FCSTD DOCUMENT  (FreeCAD 1.0R39109 (Git))
Label: 000_table_assembly
License: All rights reserved
LicenseURL: http://en.wikipedia.org/wiki/All_rights_reserved
objects: App::Link×15, App::FeaturePython×4, TechDraw::DrawProjGroupItem×4, Assembly::AssemblyLink×2, TechDraw::DrawViewDimension×2, TechDraw::DrawSVGTemplate×1, Assembly::JointGroup×1, Assembly::AssemblyObject×1, TechDraw::DrawProjGroup×1, TechDraw::DrawPage×1
note: 4 computed .brp shape members not serialized (recipe doc carries the construction recipe); baked Part::Feature solids carry a one-line shape summary decoded from their .brp
EXTERNAL_REF file=020_table_top_assembly.FCStd obj=Assembly
EXTERNAL_REF file=020_table_top_assembly.FCStd obj=Body
EXTERNAL_REF file=020_table_top_assembly.FCStd obj=Body001
EXTERNAL_REF file=020_table_top_assembly.FCStd obj=Body002
EXTERNAL_REF file=020_table_top_assembly.FCStd obj=Body003
EXTERNAL_REF file=020_table_top_assembly.FCStd obj=Body004
EXTERNAL_REF file=020_table_top_assembly.FCStd obj=Body005
EXTERNAL_REF file=040_table_bottom_assembly.FCStd obj=Assembly
EXTERNAL_REF file=040_table_bottom_assembly.FCStd obj=Body
EXTERNAL_REF file=040_table_bottom_assembly.FCStd obj=Body001
EXTERNAL_REF file=040_table_bottom_assembly.FCStd obj=Body002
EXTERNAL_REF file=040_table_bottom_assembly.FCStd obj=Body003
EXTERNAL_REF file=040_table_bottom_assembly.FCStd obj=Body004
EXTERNAL_REF file=040_table_bottom_assembly.FCStd obj=Body005
EXTERNAL_REF file=040_table_bottom_assembly.FCStd obj=Body006
EXTERNAL_REF file=040_table_bottom_assembly.FCStd obj=Body007
EXTERNAL_REF file=020_table_top_assembly.FCStd obj=Body006

FEATURE [App::Link] Body
  LinkedObject = -> <external 020_table_top_assembly.FCStd>#Body
FEATURE [App::Link] Body001
  LinkPlacement = pos=(-4.64e-14,385,70) rot=(1,0,0;1.5708rad)
  LinkedObject = -> <external 020_table_top_assembly.FCStd>#Body001
  Placement = pos=(-4.64e-14,385,70) rot=(1,0,0;1.5708rad)
FEATURE [App::Link] Body002
  LinkPlacement = pos=(-2.5e-14,-385,70) rot=(0,0.707107,-0.707107;3.14159rad)
  LinkedObject = -> <external 020_table_top_assembly.FCStd>#Body002
  Placement = pos=(-2.5e-14,-385,70) rot=(0,0.707107,-0.707107;3.14159rad)
FEATURE [App::Link] Body003
  LinkPlacement = pos=(-1085,-1.269e-13,70) rot=(0.57735,-0.57735,0.57735;4.18879rad)
  LinkedObject = -> <external 020_table_top_assembly.FCStd>#Body003
  Placement = pos=(-1085,-1.269e-13,70) rot=(0.57735,-0.57735,0.57735;4.18879rad)
FEATURE [App::Link] Body004
  LinkPlacement = pos=(1085,-7.89e-14,70) rot=(0.57735,-0.57735,0.57735;4.18879rad)
  LinkedObject = -> <external 020_table_top_assembly.FCStd>#Body004
  Placement = pos=(1085,-7.89e-14,70) rot=(0.57735,-0.57735,0.57735;4.18879rad)
FEATURE [App::Link] Body005
  LinkPlacement = pos=(-940,548.179,55) rot=(0,-0.707107,0.707107;3.14159rad)
  LinkedObject = -> <external 020_table_top_assembly.FCStd>#Body005
  Placement = pos=(-940,548.179,55) rot=(0,-0.707107,0.707107;3.14159rad)
FEATURE [App::Link] Body006
  LinkedObject = -> <external 040_table_bottom_assembly.FCStd>#Body
FEATURE [App::FeaturePython] Joint  label="Distance"  # Assembly joint (typed FeaturePython)
  Activated = true
  AngleMax = 0
  AngleMin = 0
  Detach1 = false
  Detach2 = false
  Distance = 0
  Distance2 = 0
  EnableAngleMax = false
  EnableAngleMin = false
  EnableLengthMax = false
  EnableLengthMin = false
  JointType = 5 (Distance)
  LengthMax = 0
  LengthMin = 0
  Placement1 = pos=(15,15,410) rot=(0,0,1;0rad)
  Placement2 = pos=(1.42e-14,-6.25e-14,15) rot=(0,0,1;0rad)
  Reference1 = -> Assembly [Assembly002.Body006.Face9,Assembly002.Body006.Face9]
  Reference2 = -> Assembly [Assembly001.Body.Face6,Assembly001.Body.Vertex2]
FEATURE [App::FeaturePython] Joint001  label="Distance001"  # Assembly joint (typed FeaturePython)
  Activated = true
  AngleMax = 0
  AngleMin = 0
  Detach1 = false
  Detach2 = false
  Distance = 0
  Distance2 = 0
  EnableAngleMax = false
  EnableAngleMin = false
  EnableLengthMax = false
  EnableLengthMin = false
  JointType = 5 (Distance)
  LengthMax = 0
  LengthMin = 0
  Placement1 = pos=(15,-20,355) rot=(1,0,0;1.5708rad)
  Placement2 = pos=(-1.23163,0,15) rot=(0,0,1;0rad)
  Reference1 = -> Assembly [Assembly002.Body006.Face8,Assembly002.Body006.Face8]
  Reference2 = -> Assembly [Assembly001.Body001.Face5,Assembly001.Body001.Vertex4]
FEATURE [App::FeaturePython] Joint002  label="Distance002"  # Assembly joint (typed FeaturePython)
  Activated = true
  AngleMax = 0
  AngleMin = 0
  Detach1 = false
  Detach2 = false
  Distance = 0
  Distance2 = 0
  EnableAngleMax = false
  EnableAngleMin = false
  EnableLengthMax = false
  EnableLengthMin = false
  JointType = 5 (Distance)
  LengthMax = 0
  LengthMin = 0
  Placement1 = pos=(-20,15,355) rot=(-0.57735,0.57735,0.57735;4.18879rad)
  Placement2 = pos=(5.9e-15,0,15) rot=(0,0,1;0rad)
  Reference1 = -> Assembly [Assembly002.Body006.Face7,Assembly002.Body006.Face7]
  Reference2 = -> Assembly [Assembly001.Body003.Face6,Assembly001.Body003.Vertex2]
FEATURE [App::Link] Body007
  LinkPlacement = pos=(-3.39e-14,700,-2.35e-14) rot=(0,0,1;4.71239rad)
  LinkedObject = -> <external 040_table_bottom_assembly.FCStd>#Body001
  Placement = pos=(-3.39e-14,700,-2.35e-14) rot=(0,0,1;4.71239rad)
FEATURE [App::Link] Body008
  LinkPlacement = pos=(1770,8.9e-15,1.22e-14) rot=(0,0,1;1.5708rad)
  LinkedObject = -> <external 040_table_bottom_assembly.FCStd>#Body002
  Placement = pos=(1770,8.9e-15,1.22e-14) rot=(0,0,1;1.5708rad)
FEATURE [App::Link] Body009
  LinkPlacement = pos=(1770,700,1.4038e-12) rot=(0,0,1;3.14159rad)
  LinkedObject = -> <external 040_table_bottom_assembly.FCStd>#Body003
  Placement = pos=(1770,700,1.4038e-12) rot=(0,0,1;3.14159rad)
FEATURE [TechDraw::DrawSVGTemplate] Template
  EditableTexts = approval_person=B. Hecate; creator=A. Nemesis; date_of_issue=16/08/2025; document_type=Assembly Drawing; general_tolerances=ISO 2768-m; identification_number=DN; language_code=EN; part_material=Stainless steel Mat.No. 1.4301; revision_index=AAA; sheet_number=1 / 1; sheet_scale=1 : 1; title=000_table_assembly
  Height = 297
  Orientation = 1
  Template = C:/Program Files/FreeCAD 1.0/data/Mod/TechDraw/Templates/A3_Landscape_ISO5457_minimal.svg
  Width = 420
FEATURE [App::Link] Body010
  LinkPlacement = pos=(1770,350,-260) rot=(0,-0.707107,0.707107;3.14159rad)
  LinkedObject = -> <external 040_table_bottom_assembly.FCStd>#Body004
  Placement = pos=(1770,350,-260) rot=(0,-0.707107,0.707107;3.14159rad)
FEATURE [App::Link] Body011
  LinkPlacement = pos=(2e-15,350,-260) rot=(0,-0.707107,0.707107;3.14159rad)
  LinkedObject = -> <external 040_table_bottom_assembly.FCStd>#Body005
  Placement = pos=(2e-15,350,-260) rot=(0,-0.707107,0.707107;3.14159rad)
FEATURE [App::Link] Body012
  LinkPlacement = pos=(885,-25,-260) rot=(0,1,0;1.5708rad)
  LinkedObject = -> <external 040_table_bottom_assembly.FCStd>#Body006
  Placement = pos=(885,-25,-260) rot=(0,1,0;1.5708rad)
FEATURE [App::Link] Body013
  LinkPlacement = pos=(885,725,-260) rot=(0.707107,0,-0.707107;3.14159rad)
  LinkedObject = -> <external 040_table_bottom_assembly.FCStd>#Body007
  Placement = pos=(885,725,-260) rot=(0.707107,0,-0.707107;3.14159rad)
FEATURE [Assembly::AssemblyLink] Assembly002
  Group = -> [Body006,Body007,Body008,Body009,Body010,Body011,Body012,Body013]
  LinkedObject = -> <external 040_table_bottom_assembly.FCStd>#Assembly
  Origin = -> Origin002
  Placement = pos=(-1050,350,425) rot=(1,0,0;3.14159rad)
  Rigid = true
FEATURE [App::Link] Body014
  LinkPlacement = pos=(1255.62,240,55) rot=(-0.57735,-0.57735,0.57735;2.0944rad)
  LinkedObject = -> <external 020_table_top_assembly.FCStd>#Body006
  Placement = pos=(1255.62,240,55) rot=(-0.57735,-0.57735,0.57735;2.0944rad)
FEATURE [Assembly::AssemblyLink] Assembly001
  Group = -> [Body,Body001,Body002,Body003,Body004,Body005,Body014]
  LinkedObject = -> <external 020_table_top_assembly.FCStd>#Assembly
  Origin = -> Origin001
  Rigid = true
FEATURE [App::FeaturePython] GroundedJoint  # Assembly grounded joint (typed FeaturePython)
  ObjectToGround = -> Assembly001
FEATURE [Assembly::JointGroup] Joints
  Group = -> [GroundedJoint,Joint,Joint001,Joint002]
FEATURE [Assembly::AssemblyObject] Assembly
  Group = -> [Joints,Assembly001,GroundedJoint,Assembly002,Joint,Joint001,Joint002]
  Origin = -> Origin
  Type = Assembly
FEATURE [TechDraw::DrawProjGroupItem] View  label="Front"
  CoarseView = false
  Direction = (0,-1,0)
  Focus = 100
  HardHidden = false
  IsoCount = 0
  IsoHidden = false
  IsoVisible = false
  LockPosition = true
  Perspective = false
  Rotation = 0
  RotationVector = (1,0,0)
  Scale = 0.066667
  ScaleType = 2
  ScrubCount = 1
  SeamHidden = false
  SeamVisible = true
  SmoothHidden = false
  SmoothVisible = true
  Source = -> [Assembly]
  Type = 0
  X = 0
  XDirection = (-1,0,-1e-16)
  Y = 0
FEATURE [TechDraw::DrawProjGroupItem] ProjItem  label="Right"
  CoarseView = false
  Direction = (-1,-1e-16,-1e-16)
  Focus = 100
  HardHidden = false
  IsoCount = 0
  IsoHidden = false
  IsoVisible = false
  LockPosition = false
  Perspective = false
  Rotation = 0
  RotationVector = (1,0,0)
  Scale = 0.066667
  ScaleType = 0
  ScrubCount = 1
  SeamHidden = false
  SeamVisible = true
  SmoothHidden = false
  SmoothVisible = true
  Source = -> [Assembly]
  Type = 2
  X = -128.127
  XDirection = (-1e-16,1,0)
  Y = 0
FEATURE [TechDraw::DrawProjGroupItem] ProjItem001  label="Left"
  CoarseView = false
  Direction = (1,-1e-16,1e-16)
  Focus = 100
  HardHidden = false
  IsoCount = 0
  IsoHidden = false
  IsoVisible = false
  LockPosition = false
  Perspective = false
  Rotation = 0
  RotationVector = (1,0,0)
  ScaleType = 0
  ScrubCount = 1
  SeamHidden = false
  SeamVisible = true
  SmoothHidden = false
  SmoothVisible = true
  Source = -> [Assembly]
  Type = 1
  X = 128.127
  XDirection = (-1e-16,-1,0)
  Y = 0
FEATURE [TechDraw::DrawProjGroupItem] ProjItem002  label="Bottom"
  CoarseView = false
  Direction = (-1e-16,0,1)
  Focus = 100
  HardHidden = false
  IsoCount = 0
  IsoHidden = false
  IsoVisible = false
  LockPosition = false
  Perspective = false
  Rotation = 0
  RotationVector = (1,0,0)
  ScaleType = 0
  ScrubCount = 1
  SeamHidden = false
  SeamVisible = true
  SmoothHidden = false
  SmoothVisible = true
  Source = -> [Assembly]
  Type = 5
  X = 0
  XDirection = (-1,0,-1e-16)
  Y = 76.4396
FEATURE [TechDraw::DrawProjGroup] ProjGroup
  Anchor = -> View
  AutoDistribute = true
  LockPosition = false
  ProjectionType = 0
  Rotation = 0
  Scale = 0.066667
  ScaleType = 2
  Source = -> [Assembly]
  Views = -> [View,ProjItem,ProjItem001,ProjItem002]
  X = 210.506
  Y = 148.5
  spacingX = 15
  spacingY = 15
FEATURE [TechDraw::DrawViewDimension] Dimension
  AngleOverride = false
  Arbitrary = false
  ArbitraryTolerances = false
  BoxCorners = (2) [(-73.3337,-28.3335,0),(73.3337,28.3335,0)]
  EqualTolerance = true
  ExtensionAngle = 0
  FormatSpec = %.2w
  FormatSpecOverTolerance = %+.2w
  FormatSpecUnderTolerance = %+.2w
  Inverted = false
  LineAngle = 0
  LockPosition = false
  MeasureType = 1
  OverTolerance = 0
  References2D = -> [View]
  Rotation = 0
  ScaleType = 0
  TheoreticalExact = false
  Type = 0
  UnderTolerance = 0
  X = 16.6095
  Y = -44.1973
FEATURE [TechDraw::DrawViewDimension] Dimension001
  AngleOverride = false
  Arbitrary = false
  ArbitraryTolerances = false
  BoxCorners = (2) [(-33.1061,-28.3335,0),(33.1061,28.3335,0)]
  EqualTolerance = true
  ExtensionAngle = 0
  FormatSpec = %.2w
  FormatSpecOverTolerance = %+.2w
  FormatSpecUnderTolerance = %+.2w
  Inverted = false
  LineAngle = 0
  LockPosition = false
  MeasureType = 1
  OverTolerance = 0
  References2D = -> [ProjItem001]
  Rotation = 0
  ScaleType = 0
  TheoreticalExact = false
  Type = 0
  UnderTolerance = 0
  X = 9.5557
  Y = -44.5532
FEATURE [TechDraw::DrawPage] Page
  KeepUpdated = true
  NextBalloonIndex = 1
  ProjectionType = 0
  Template = -> Template
  Views = -> [ProjGroup,Dimension,Dimension001]

RESOLVED EXTERNAL PARTS (link-assembly join: the EXTERNAL_REF files above that resolve inside this repo's crawl, each included once):
---- part 020_table_top_assembly.FCStd = doc fcstd_f8d654153843 ----
FCSTD DOCUMENT  (FreeCAD 1.0R39109 (Git))
Label: 020_table_top_assembly
License: All rights reserved
LicenseURL: http://en.wikipedia.org/wiki/All_rights_reserved
objects: App::FeaturePython×17, App::Link×7, Assembly::JointGroup×1, Assembly::AssemblyObject×1
EXTERNAL_REF file=021_table_top_sheet_30mm.FCStd obj=Body
EXTERNAL_REF file=022_table_frame_front.FCStd obj=Body
EXTERNAL_REF file=023_table_frame_back.FCStd obj=Body
EXTERNAL_REF file=025_table_frame_side_left.FCStd obj=Body
EXTERNAL_REF file=026_table_frame_side_right.FCStd obj=Body
EXTERNAL_REF file=028_table_clamp.FCStd obj=Body

FEATURE [App::Link] Body
  LinkedObject = -> <external 021_table_top_sheet_30mm.FCStd>#Body
FEATURE [App::FeaturePython] GroundedJoint  # Assembly grounded joint (typed FeaturePython)
  ObjectToGround = -> Body
FEATURE [App::Link] Body001
  LinkPlacement = pos=(-4.64e-14,385,70) rot=(1,0,0;1.5708rad)
  LinkedObject = -> <external 022_table_frame_front.FCStd>#Body
  Placement = pos=(-4.64e-14,385,70) rot=(1,0,0;1.5708rad)
FEATURE [App::Link] Body002
  LinkPlacement = pos=(-2.5e-14,-385,70) rot=(0,0.707107,-0.707107;3.14159rad)
  LinkedObject = -> <external 023_table_frame_back.FCStd>#Body
  Placement = pos=(-2.5e-14,-385,70) rot=(0,0.707107,-0.707107;3.14159rad)
FEATURE [App::FeaturePython] Joint002  label="Back1"  # Assembly joint (typed FeaturePython)
  Activated = true
  AngleMax = 0
  AngleMin = 0
  Detach1 = false
  Detach2 = false
  Distance = 0
  Distance2 = 0
  EnableAngleMax = false
  EnableAngleMin = false
  EnableLengthMax = false
  EnableLengthMin = false
  JointType = 5 (Distance)
  LengthMax = 0
  LengthMin = 0
  Placement1 = pos=(1100,-6.39e-14,-4e-16) rot=(-0.57735,-0.57735,0.57735;2.0944rad)
  Placement2 = pos=(-1100,0,0) rot=(0.57735,-0.57735,0.57735;4.18879rad)
  Reference1 = -> Assembly [Body.Face3,Body.Vertex8]
  Reference2 = -> Assembly [Body002.Face1,Body002.Face1]
FEATURE [App::FeaturePython] Joint  label="Back2"  # Assembly joint (typed FeaturePython)
  Activated = true
  AngleMax = 0
  AngleMin = 0
  Detach1 = false
  Detach2 = false
  Distance = 0
  Distance2 = 0
  EnableAngleMax = false
  EnableAngleMin = false
  EnableLengthMax = false
  EnableLengthMin = false
  JointType = 5 (Distance)
  LengthMax = 0
  LengthMin = 0
  Placement1 = pos=(1.38088,55,-0.0189681) rot=(0,-0.707107,0.707107;3.14159rad)
  Placement2 = pos=(1.42e-14,-6.25e-14,15) rot=(0,0,1;0rad)
  Reference1 = -> Assembly [Body002.Face2,Body002.Vertex7]
  Reference2 = -> Assembly [Body.Face6,Body.Vertex6]
FEATURE [App::FeaturePython] Joint003  label="Back3"  # Assembly joint (typed FeaturePython)
  Activated = true
  AngleMax = 0
  AngleMin = 0
  Detach1 = false
  Detach2 = false
  Distance = 0
  Distance2 = 0
  EnableAngleMax = false
  EnableAngleMin = false
  EnableLengthMax = false
  EnableLengthMin = false
  JointType = 5 (Distance)
  LengthMax = 0
  LengthMin = 0
  Placement1 = pos=(-1010,0,15) rot=(0,0,1;0rad)
  Placement2 = pos=(-5.37e-14,-400,-4e-16) rot=(-1,0,0;1.5708rad)
  Reference1 = -> Assembly [Body002.Face5,Body002.Face5]
  Reference2 = -> Assembly [Body.Face2,Body.Vertex6]
FEATURE [App::FeaturePython] Joint004  label="Front1"  # Assembly joint (typed FeaturePython)
  Activated = true
  AngleMax = 0
  AngleMin = 0
  Detach1 = false
  Detach2 = false
  Distance = 0
  Distance2 = 0
  EnableAngleMax = false
  EnableAngleMin = false
  EnableLengthMax = false
  EnableLengthMin = false
  JointType = 5 (Distance)
  LengthMax = 0
  LengthMin = 0
  Placement1 = pos=(-3.13e-14,-55,0) rot=(-1,0,0;1.5708rad)
  Placement2 = pos=(1.42e-14,-6.25e-14,15) rot=(0,0,1;0rad)
  Reference1 = -> Assembly [Body001.Face3,Body001.Vertex4]
  Reference2 = -> Assembly [Body.Face6,Body.Vertex8]
FEATURE [App::FeaturePython] Joint005  label="Front2"  # Assembly joint (typed FeaturePython)
  Activated = true
  AngleMax = 0
  AngleMin = 0
  Detach1 = false
  Detach2 = false
  Distance = 0
  Distance2 = 0
  EnableAngleMax = false
  EnableAngleMin = false
  EnableLengthMax = false
  EnableLengthMin = false
  JointType = 5 (Distance)
  LengthMax = 0
  LengthMin = 0
  Placement1 = pos=(5.37e-14,400,-4e-16) rot=(0,-0.707107,0.707107;3.14159rad)
  Placement2 = pos=(-1.23163,0,-15) rot=(0,0,1;0rad)
  Reference1 = -> Assembly [Body.Face4,Body.Vertex7]
  Reference2 = -> Assembly [Body001.Face4,Body001.Edge5]
FEATURE [App::FeaturePython] Joint006  label="Front3"  # Assembly joint (typed FeaturePython)
  Activated = true
  AngleMax = 0
  AngleMin = 0
  Detach1 = false
  Detach2 = false
  Distance = 0
  Distance2 = 0
  EnableAngleMax = false
  EnableAngleMin = false
  EnableLengthMax = false
  EnableLengthMin = false
  JointType = 5 (Distance)
  LengthMax = 0
  LengthMin = 0
  Placement1 = pos=(1100,-6.39e-14,-4e-16) rot=(-0.57735,-0.57735,0.57735;2.0944rad)
  Placement2 = pos=(1100,0,0) rot=(-0.57735,-0.57735,0.57735;2.0944rad)
  Reference1 = -> Assembly [Body.Face3,Body.Vertex7]
  Reference2 = -> Assembly [Body001.Face6,Body001.Face6]
FEATURE [App::Link] Body003
  LinkPlacement = pos=(-1085,-1.269e-13,70) rot=(0.57735,-0.57735,0.57735;4.18879rad)
  LinkedObject = -> <external 025_table_frame_side_left.FCStd>#Body
  Placement = pos=(-1085,-1.269e-13,70) rot=(0.57735,-0.57735,0.57735;4.18879rad)
FEATURE [App::FeaturePython] Joint008  label="Left1"  # Assembly joint (typed FeaturePython)
  Activated = true
  AngleMax = 0
  AngleMin = 0
  Detach1 = false
  Detach2 = false
  Distance = 0
  Distance2 = 0
  EnableAngleMax = false
  EnableAngleMin = false
  EnableLengthMax = false
  EnableLengthMin = false
  JointType = 5 (Distance)
  LengthMax = 0
  LengthMin = 0
  Placement1 = pos=(-3.9e-15,55,0) rot=(0,-0.707107,0.707107;3.14159rad)
  Placement2 = pos=(1.42e-14,-6.25e-14,15) rot=(0,0,1;0rad)
  Reference1 = -> Assembly [Body003.Face4,Body003.Face4]
  Reference2 = -> Assembly [Body.Face6,Body.Vertex4]
FEATURE [App::FeaturePython] Joint009  label="Left2"  # Assembly joint (typed FeaturePython)
  Activated = true
  AngleMax = 0
  AngleMin = 0
  Detach1 = false
  Detach2 = false
  Distance = 0
  Distance2 = 0
  EnableAngleMax = false
  EnableAngleMin = false
  EnableLengthMax = false
  EnableLengthMin = false
  JointType = 5 (Distance)
  LengthMax = 0
  LengthMin = 0
  Placement1 = pos=(-2.1e-15,0,-15) rot=(0,0,1;0rad)
  Placement2 = pos=(-1100,-4.97e-14,-4e-16) rot=(0.57735,-0.57735,0.57735;4.18879rad)
  Reference1 = -> Assembly [Body003.Face5,Body003.Vertex7]
  Reference2 = -> Assembly [Body.Face1,Body.Face1]
FEATURE [App::FeaturePython] Joint010  label="Left3"  # Assembly joint (typed FeaturePython)
  Activated = true
  AngleMax = 0
  AngleMin = 0
  Detach1 = false
  Detach2 = false
  Distance = 0
  Distance2 = 0
  EnableAngleMax = false
  EnableAngleMin = false
  EnableLengthMax = false
  EnableLengthMin = false
  JointType = 5 (Distance)
  LengthMax = 0
  LengthMin = 0
  Placement1 = pos=(370,-1.42e-14,0) rot=(-0.57735,-0.57735,0.57735;2.0944rad)
  Placement2 = pos=(-5e-15,0,-15) rot=(0,0,1;0rad)
  Reference1 = -> Assembly [Body003.Face3,Body003.Vertex6]
  Reference2 = -> Assembly [Body002.Face4,Body002.Vertex5]
FEATURE [App::Link] Body004
  LinkPlacement = pos=(1085,-7.89e-14,70) rot=(0.57735,-0.57735,0.57735;4.18879rad)
  LinkedObject = -> <external 026_table_frame_side_right.FCStd>#Body
  Placement = pos=(1085,-7.89e-14,70) rot=(0.57735,-0.57735,0.57735;4.18879rad)
FEATURE [App::FeaturePython] Joint011  label="Right1"  # Assembly joint (typed FeaturePython)
  Activated = true
  AngleMax = 0
  AngleMin = 0
  Detach1 = false
  Detach2 = false
  Distance = 0
  Distance2 = 0
  EnableAngleMax = false
  EnableAngleMin = false
  EnableLengthMax = false
  EnableLengthMin = false
  JointType = 5 (Distance)
  LengthMax = 0
  LengthMin = 0
  Placement1 = pos=(-4.9e-15,55,0) rot=(0,0.707107,-0.707107;3.14159rad)
  Placement2 = pos=(1.42e-14,-6.25e-14,15) rot=(0,0,1;0rad)
  Reference1 = -> Assembly [Body004.Face4,Body004.Vertex2]
  Reference2 = -> Assembly [Body.Face6,Body.Vertex6]
FEATURE [App::FeaturePython] Joint012  label="Right2"  # Assembly joint (typed FeaturePython)
  Activated = true
  AngleMax = 0
  AngleMin = 0
  Detach1 = false
  Detach2 = false
  Distance = 0
  Distance2 = 0
  EnableAngleMax = false
  EnableAngleMin = false
  EnableLengthMax = false
  EnableLengthMin = false
  JointType = 5 (Distance)
  LengthMax = 0
  LengthMin = 0
  Placement1 = pos=(3.7e-15,0,15) rot=(0,0,1;0rad)
  Placement2 = pos=(1100,-6.39e-14,-4e-16) rot=(-0.57735,-0.57735,0.57735;2.0944rad)
  Reference1 = -> Assembly [Body004.Face6,Body004.Vertex2]
  Reference2 = -> Assembly [Body.Face3,Body.Face3]
FEATURE [App::FeaturePython] Joint013  label="Right3"  # Assembly joint (typed FeaturePython)
  Activated = true
  AngleMax = 0
  AngleMin = 0
  Detach1 = false
  Detach2 = false
  Distance = 0
  Distance2 = 0
  EnableAngleMax = false
  EnableAngleMin = false
  EnableLengthMax = false
  EnableLengthMin = false
  JointType = 5 (Distance)
  LengthMax = 0
  LengthMin = 0
  Placement1 = pos=(-370,0,0) rot=(-0.57735,0.57735,-0.57735;2.0944rad)
  Placement2 = pos=(-1.23163,0,15) rot=(0,0,1;0rad)
  Reference1 = -> Assembly [Body004.Face1,Body004.Face1]
  Reference2 = -> Assembly [Body001.Face5,Body001.Vertex10]
FEATURE [App::Link] Body005
  LinkPlacement = pos=(-940,548.179,55) rot=(0,-0.707107,0.707107;3.14159rad)
  LinkedObject = -> <external 028_table_clamp.FCStd>#Body
  Placement = pos=(-940,548.179,55) rot=(0,-0.707107,0.707107;3.14159rad)
FEATURE [App::FeaturePython] Joint014  label="Distance"  # Assembly joint (typed FeaturePython)
  Activated = true
  AngleMax = 0
  AngleMin = 0
  Detach1 = false
  Detach2 = false
  Distance = 0
  Distance2 = 0
  EnableAngleMax = false
  EnableAngleMin = false
  EnableLengthMax = false
  EnableLengthMin = false
  JointType = 5 (Distance)
  LengthMax = 0
  LengthMin = 0
  Placement1 = pos=(0,70,0) rot=(0,-0.707107,0.707107;3.14159rad)
  Placement2 = pos=(1.42e-14,-6.25e-14,-15) rot=(0,0,1;0rad)
  Reference1 = -> Assembly [Body005.Face4,Body005.Face4]
  Reference2 = -> Assembly [Body.Face5,Body.Vertex1]
FEATURE [App::FeaturePython] Joint015  label="Distance001"  # Assembly joint (typed FeaturePython)
  Activated = true
  AngleMax = 0
  AngleMin = 0
  Detach1 = false
  Detach2 = false
  Distance = 0
  Distance2 = 0
  EnableAngleMax = false
  EnableAngleMin = false
  EnableLengthMax = false
  EnableLengthMin = false
  JointType = 5 (Distance)
  LengthMax = 0
  LengthMin = 0
  Placement1 = pos=(-1100,0,0) rot=(-0.57735,0.57735,-0.57735;2.0944rad)
  Placement2 = pos=(160,0,0) rot=(-0.57735,-0.57735,0.57735;2.0944rad)
  Reference1 = -> Assembly [Body001.Face1,Body001.Vertex4]
  Reference2 = -> Assembly [Body005.Face3,Body005.Face3]
FEATURE [App::Link] Body006
  LinkPlacement = pos=(1255.62,240,55) rot=(-0.57735,-0.57735,0.57735;2.0944rad)
  LinkedObject = -> <external 028_table_clamp.FCStd>#Body
  Placement = pos=(1255.62,240,55) rot=(-0.57735,-0.57735,0.57735;2.0944rad)
FEATURE [App::FeaturePython] Joint016  label="Distance002"  # Assembly joint (typed FeaturePython)
  Activated = true
  AngleMax = 0
  AngleMin = 0
  Detach1 = false
  Detach2 = false
  Distance = 0
  Distance2 = 0
  EnableAngleMax = false
  EnableAngleMin = false
  EnableLengthMax = false
  EnableLengthMin = false
  JointType = 5 (Distance)
  LengthMax = 0
  LengthMin = 0
  Placement1 = pos=(160,0,0) rot=(-0.57735,-0.57735,0.57735;2.0944rad)
  Placement2 = pos=(-1.23163,0,-15) rot=(0,0,1;0rad)
  Reference1 = -> Assembly [Body006.Face3,Body006.Vertex8]
  Reference2 = -> Assembly [Body001.Face4,Body001.Edge5]
FEATURE [App::FeaturePython] Joint017  label="Distance003"  # Assembly joint (typed FeaturePython)
  Activated = true
  AngleMax = 0
  AngleMin = 0
  Detach1 = false
  Detach2 = false
  Distance = 0
  Distance2 = 0
  EnableAngleMax = false
  EnableAngleMin = false
  EnableLengthMax = false
  EnableLengthMin = false
  JointType = 5 (Distance)
  LengthMax = 0
  LengthMin = 0
  Placement1 = pos=(0,70,0) rot=(0,-0.707107,0.707107;3.14159rad)
  Placement2 = pos=(1.42e-14,-6.25e-14,-15) rot=(0,0,1;0rad)
  Reference1 = -> Assembly [Body006.Face4,Body006.Face4]
  Reference2 = -> Assembly [Body.Face5,Body.Vertex7]
FEATURE [Assembly::JointGroup] Joints
  Group = -> [GroundedJoint,Joint002,Joint,Joint003,Joint004,Joint005,Joint006,Joint008,Joint009,Joint010,Joint011,Joint012,Joint013,Joint014,Joint015,Joint016,Joint017]
FEATURE [Assembly::AssemblyObject] Assembly
  Group = -> [Joints,Body,GroundedJoint,Body001,Body002,Joint002,Joint,Joint003,Joint004,Joint005,Joint006,Body003,Joint008,Joint009,Joint010,Body004,Joint011,Joint012,Joint013,Body005,Joint014,Joint015,Body006,Joint016,Joint017]
  Origin = -> Origin
  Type = Assembly
---- part 040_table_bottom_assembly.FCStd = doc fcstd_6b884d282858 ----
FCSTD DOCUMENT  (FreeCAD 1.0R39109 (Git))
Label: 040_table_bottom_assembly
License: All rights reserved
LicenseURL: http://en.wikipedia.org/wiki/All_rights_reserved
objects: App::FeaturePython×22, App::Link×8, Assembly::JointGroup×1, Assembly::AssemblyObject×1
EXTERNAL_REF file=042_table_bottom_leg_back_left.FCStd obj=Body
EXTERNAL_REF file=043_table_bottom_leg_front_right.FCStd obj=Body
EXTERNAL_REF file=044_table_bottom_leg_back_right.FCStd obj=Body
EXTERNAL_REF file=045_table_bottom_frame_small.FCStd obj=Body
EXTERNAL_REF file=046_table_bottom_frame_large.FCStd obj=Body

FEATURE [App::Link] Body
  LinkedObject = -> <external 042_table_bottom_leg_back_left.FCStd>#Body
FEATURE [App::FeaturePython] GroundedJoint  # Assembly grounded joint (typed FeaturePython)
  ObjectToGround = -> Body
FEATURE [App::Link] Body001
  LinkPlacement = pos=(-3.39e-14,700,-2.35e-14) rot=(0,0,1;4.71239rad)
  LinkedObject = -> <external 042_table_bottom_leg_back_left.FCStd>#Body
  Placement = pos=(-3.39e-14,700,-2.35e-14) rot=(0,0,1;4.71239rad)
FEATURE [App::FeaturePython] Joint  label="Legt Left Back 1"  # Assembly joint (typed FeaturePython)
  Activated = true
  AngleMax = 0
  AngleMin = 0
  Detach1 = false
  Detach2 = false
  Distance = -600
  Distance2 = 0
  EnableAngleMax = false
  EnableAngleMin = false
  EnableLengthMax = false
  EnableLengthMin = false
  JointType = 5 (Distance)
  LengthMax = 0
  LengthMin = 0
  Placement1 = pos=(50,1.4676,-14.8856) rot=(-0.57735,-0.57735,0.57735;2.0944rad)
  Placement2 = pos=(1.4676,50,-14.8856) rot=(0,-0.707107,0.707107;3.14159rad)
  Reference1 = -> Assembly [Body001.Face6,Body001.Face6]
  Reference2 = -> Assembly [Body.Face5,Body.Face5]
FEATURE [App::FeaturePython] Joint001  label="Legt Left Back 2"  # Assembly joint (typed FeaturePython)
  Activated = true
  AngleMax = 0
  AngleMin = 0
  Detach1 = false
  Detach2 = false
  Distance = 0
  Distance2 = 0
  EnableAngleMax = false
  EnableAngleMin = false
  EnableLengthMax = false
  EnableLengthMin = false
  JointType = 5 (Distance)
  LengthMax = 0
  LengthMin = 0
  Placement1 = pos=(15,15,410) rot=(0,0,1;0rad)
  Placement2 = pos=(15,15,410) rot=(0,0,1;0rad)
  Reference1 = -> Assembly [Body001.Face9,Body001.Face9]
  Reference2 = -> Assembly [Body.Face9,Body.Face9]
FEATURE [App::FeaturePython] Joint002  label="Legt Left Back 3"  # Assembly joint (typed FeaturePython)
  Activated = true
  AngleMax = 0
  AngleMin = 0
  Detach1 = false
  Detach2 = false
  Distance = 0
  Distance2 = 0
  EnableAngleMax = false
  EnableAngleMin = false
  EnableLengthMax = false
  EnableLengthMin = false
  JointType = 5 (Distance)
  LengthMax = 0
  LengthMin = 0
  Placement1 = pos=(-50,9e-16,-55) rot=(0.57735,-0.57735,0.57735;4.18879rad)
  Placement2 = pos=(0,-50,-55) rot=(-1,0,0;1.5708rad)
  Reference1 = -> Assembly [Body.Face1,Body.Face1]
  Reference2 = -> Assembly [Body001.Face3,Body001.Vertex3]
FEATURE [App::Link] Body002
  LinkPlacement = pos=(1770,8.9e-15,1.22e-14) rot=(0,0,1;1.5708rad)
  LinkedObject = -> <external 043_table_bottom_leg_front_right.FCStd>#Body
  Placement = pos=(1770,8.9e-15,1.22e-14) rot=(0,0,1;1.5708rad)
FEATURE [App::FeaturePython] Joint003  label="Leg Right Front 1"  # Assembly joint (typed FeaturePython)
  Activated = true
  AngleMax = 0
  AngleMin = 0
  Detach1 = false
  Detach2 = false
  Distance = 0
  Distance2 = 0
  EnableAngleMax = false
  EnableAngleMin = false
  EnableLengthMax = false
  EnableLengthMin = false
  JointType = 5 (Distance)
  LengthMax = 0
  LengthMin = 0
  Placement1 = pos=(-2e-16,0,-410) rot=(0,0,1;0rad)
  Placement2 = pos=(0,0,-410) rot=(0,0,1;0rad)
  Reference1 = -> Assembly [Body.Face2,Body.Face2]
  Reference2 = -> Assembly [Body002.Face2,Body002.Face2]
FEATURE [App::FeaturePython] Joint004  label="Leg Right Front 2"  # Assembly joint (typed FeaturePython)
  Activated = true
  AngleMax = 0
  AngleMin = 0
  Detach1 = false
  Detach2 = false
  Distance = 0
  Distance2 = 0
  EnableAngleMax = false
  EnableAngleMin = false
  EnableLengthMax = false
  EnableLengthMin = false
  JointType = 5 (Distance)
  LengthMax = 0
  LengthMin = 0
  Placement1 = pos=(-9e-16,-50,-55) rot=(-1,0,0;1.5708rad)
  Placement2 = pos=(-50,0,-55) rot=(-0.57735,0.57735,-0.57735;2.0944rad)
  Reference1 = -> Assembly [Body.Face3,Body.Face3]
  Reference2 = -> Assembly [Body002.Face1,Body002.Vertex4]
FEATURE [App::FeaturePython] Joint005  label="Leg Right Front 3"  # Assembly joint (typed FeaturePython)
  Activated = true
  AngleMax = 0
  AngleMin = 0
  Detach1 = false
  Detach2 = false
  Distance = -1670
  Distance2 = 0
  EnableAngleMax = false
  EnableAngleMin = false
  EnableLengthMax = false
  EnableLengthMin = false
  JointType = 5 (Distance)
  LengthMax = 0
  LengthMin = 0
  Placement1 = pos=(50,1.4676,-14.8856) rot=(-0.57735,-0.57735,0.57735;2.0944rad)
  Placement2 = pos=(1.4676,50,-14.8856) rot=(0,-0.707107,0.707107;3.14159rad)
  Reference1 = -> Assembly [Body.Face6,Body.Face6]
  Reference2 = -> Assembly [Body002.Face5,Body002.Face5]
FEATURE [App::Link] Body003
  LinkPlacement = pos=(1770,700,1.4038e-12) rot=(0,0,1;3.14159rad)
  LinkedObject = -> <external 044_table_bottom_leg_back_right.FCStd>#Body
  Placement = pos=(1770,700,1.4038e-12) rot=(0,0,1;3.14159rad)
FEATURE [App::FeaturePython] Joint006  label="Leg Right Back 1"  # Assembly joint (typed FeaturePython)
  Activated = true
  AngleMax = 0
  AngleMin = 0
  Detach1 = false
  Detach2 = false
  Distance = 0
  Distance2 = 0
  EnableAngleMax = false
  EnableAngleMin = false
  EnableLengthMax = false
  EnableLengthMin = false
  JointType = 5 (Distance)
  LengthMax = 0
  LengthMin = 0
  Placement1 = pos=(0,0,-410) rot=(0,0,1;0rad)
  Placement2 = pos=(-2e-16,0,-410) rot=(0,0,1;0rad)
  Reference1 = -> Assembly [Body003.Face2,Body003.Face2]
  Reference2 = -> Assembly [Body.Face2,Body.Face2]
FEATURE [App::FeaturePython] Joint007  label="Leg Right Back 2"  # Assembly joint (typed FeaturePython)
  Activated = true
  AngleMax = 0
  AngleMin = 0
  Detach1 = false
  Detach2 = false
  Distance = 0
  Distance2 = 0
  EnableAngleMax = false
  EnableAngleMin = false
  EnableLengthMax = false
  EnableLengthMin = false
  JointType = 5 (Distance)
  LengthMax = 0
  LengthMin = 0
  Placement1 = pos=(0,-50,-55) rot=(-1,0,0;1.5708rad)
  Placement2 = pos=(-50,1e-15,-55) rot=(0.57735,-0.57735,0.57735;4.18879rad)
  Reference1 = -> Assembly [Body003.Face3,Body003.Face3]
  Reference2 = -> Assembly [Body001.Face1,Body001.Vertex1]
FEATURE [App::FeaturePython] Joint008  label="Leg Right Back 3"  # Assembly joint (typed FeaturePython)
  Activated = true
  AngleMax = 0
  AngleMin = 0
  Detach1 = false
  Detach2 = false
  Distance = -1670
  Distance2 = 0
  EnableAngleMax = false
  EnableAngleMin = false
  EnableLengthMax = false
  EnableLengthMin = false
  JointType = 5 (Distance)
  LengthMax = 0
  LengthMin = 0
  Placement1 = pos=(1.4676,50,-14.8856) rot=(0,-0.707107,0.707107;3.14159rad)
  Placement2 = pos=(50,1.4676,-14.8856) rot=(-0.57735,-0.57735,0.57735;2.0944rad)
  Reference1 = -> Assembly [Body001.Face5,Body001.Face5]
  Reference2 = -> Assembly [Body003.Face6,Body003.Face6]
FEATURE [App::Link] Body004
  LinkPlacement = pos=(1770,350,-260) rot=(0,-0.707107,0.707107;3.14159rad)
  LinkedObject = -> <external 045_table_bottom_frame_small.FCStd>#Body
  Placement = pos=(1770,350,-260) rot=(0,-0.707107,0.707107;3.14159rad)
FEATURE [App::Link] Body005
  LinkPlacement = pos=(2e-15,350,-260) rot=(0,-0.707107,0.707107;3.14159rad)
  LinkedObject = -> <external 045_table_bottom_frame_small.FCStd>#Body
  Placement = pos=(2e-15,350,-260) rot=(0,-0.707107,0.707107;3.14159rad)
FEATURE [App::FeaturePython] Joint009  label="Distance"  # Assembly joint (typed FeaturePython)
  Activated = true
  AngleMax = 0
  AngleMin = 0
  Detach1 = false
  Detach2 = false
  Distance = 0
  Distance2 = 0
  EnableAngleMax = false
  EnableAngleMin = false
  EnableLengthMax = false
  EnableLengthMin = false
  JointType = 5 (Distance)
  LengthMax = 0
  LengthMin = 0
  Placement1 = pos=(2.274e-13,-5.68e-14,300) rot=(0,0,1;0rad)
  Placement2 = pos=(50,1.4676,-14.8856) rot=(-0.57735,-0.57735,0.57735;2.0944rad)
  Reference1 = -> Assembly [Body004.Face6,Body004.Face6]
  Reference2 = -> Assembly [Body002.Face6,Body002.Face6]
FEATURE [App::FeaturePython] Joint010  label="Distance001"  # Assembly joint (typed FeaturePython)
  Activated = true
  AngleMax = 0
  AngleMin = 0
  Detach1 = false
  Detach2 = false
  Distance = 0
  Distance2 = 0
  EnableAngleMax = false
  EnableAngleMin = false
  EnableLengthMax = false
  EnableLengthMin = false
  JointType = 5 (Distance)
  LengthMax = 0
  LengthMin = 0
  Placement1 = pos=(4e-16,-50,-55) rot=(-1,0,0;1.5708rad)
  Placement2 = pos=(-50,0,0) rot=(-0.57735,0.57735,-0.57735;2.0944rad)
  Reference1 = -> Assembly [Body002.Face3,Body002.Face3]
  Reference2 = -> Assembly [Body004.Face1,Body004.Vertex2]
FEATURE [App::FeaturePython] Joint011  label="Distance002"  # Assembly joint (typed FeaturePython)
  Activated = true
  AngleMax = 0
  AngleMin = 0
  Detach1 = false
  Detach2 = false
  Distance = -100
  Distance2 = 0
  EnableAngleMax = false
  EnableAngleMin = false
  EnableLengthMax = false
  EnableLengthMin = false
  JointType = 5 (Distance)
  LengthMax = 0
  LengthMin = 0
  Placement1 = pos=(0,50,5.68e-14) rot=(0,0.707107,-0.707107;3.14159rad)
  Placement2 = pos=(0,0,-410) rot=(0,0,1;0rad)
  Reference1 = -> Assembly [Body004.Face4,Body004.Vertex8]
  Reference2 = -> Assembly [Body002.Face2,Body002.Face2]
FEATURE [App::FeaturePython] Joint012  label="Distance003"  # Assembly joint (typed FeaturePython)
  Activated = true
  AngleMax = 0
  AngleMin = 0
  Detach1 = false
  Detach2 = false
  Distance = 0
  Distance2 = 0
  EnableAngleMax = false
  EnableAngleMin = false
  EnableLengthMax = false
  EnableLengthMin = false
  JointType = 5 (Distance)
  LengthMax = 0
  LengthMin = 0
  Placement1 = pos=(5e-16,0,300) rot=(0,0,1;0rad)
  Placement2 = pos=(1.4676,50,-14.8856) rot=(0,-0.707107,0.707107;3.14159rad)
  Reference1 = -> Assembly [Body005.Face6,Body005.Vertex4]
  Reference2 = -> Assembly [Body.Face5,Body.Vertex1]
FEATURE [App::FeaturePython] Joint013  label="Distance004"  # Assembly joint (typed FeaturePython)
  Activated = true
  AngleMax = 0
  AngleMin = 0
  Detach1 = false
  Detach2 = false
  Distance = 0
  Distance2 = 0
  EnableAngleMax = false
  EnableAngleMin = false
  EnableLengthMax = false
  EnableLengthMin = false
  JointType = 5 (Distance)
  LengthMax = 0
  LengthMin = 0
  Placement1 = pos=(-50,5.68e-14,0) rot=(-0.57735,0.57735,-0.57735;2.0944rad)
  Placement2 = pos=(50,1.4676,-14.8856) rot=(-0.57735,-0.57735,0.57735;2.0944rad)
  Reference1 = -> Assembly [Body005.Face1,Body005.Vertex4]
  Reference2 = -> Assembly [Body.Face6,Body.Face6]
FEATURE [App::FeaturePython] Joint014  label="Distance005"  # Assembly joint (typed FeaturePython)
  Activated = true
  AngleMax = 0
  AngleMin = 0
  Detach1 = false
  Detach2 = false
  Distance = 0
  Distance2 = 0
  EnableAngleMax = false
  EnableAngleMin = false
  EnableLengthMax = false
  EnableLengthMin = false
  JointType = 5 (Distance)
  LengthMax = 0
  LengthMin = 0
  Placement1 = pos=(-2e-16,-50,0) rot=(1,0,0;4.71239rad)
  Placement2 = pos=(-2.274e-13,-50,0) rot=(1,0,0;4.71239rad)
  Reference1 = -> Assembly [Body005.Face2,Body005.Vertex4]
  Reference2 = -> Assembly [Body004.Face2,Body004.Vertex3]
FEATURE [App::Link] Body006
  LinkPlacement = pos=(885,-25,-260) rot=(0,1,0;1.5708rad)
  LinkedObject = -> <external 046_table_bottom_frame_large.FCStd>#Body
  Placement = pos=(885,-25,-260) rot=(0,1,0;1.5708rad)
FEATURE [App::Link] Body007
  LinkPlacement = pos=(885,725,-260) rot=(0.707107,0,-0.707107;3.14159rad)
  LinkedObject = -> <external 046_table_bottom_frame_large.FCStd>#Body
  Placement = pos=(885,725,-260) rot=(0.707107,0,-0.707107;3.14159rad)
FEATURE [App::FeaturePython] Joint015  label="Distance006"  # Assembly joint (typed FeaturePython)
  Activated = true
  AngleMax = 0
  AngleMin = 0
  Detach1 = false
  Detach2 = false
  Distance = 0
  Distance2 = 0
  EnableAngleMax = false
  EnableAngleMin = false
  EnableLengthMax = false
  EnableLengthMin = false
  JointType = 5 (Distance)
  LengthMax = 0
  LengthMin = 0
  Placement1 = pos=(0,0,835) rot=(0,0,1;0rad)
  Placement2 = pos=(1.4676,50,-14.8856) rot=(0,-0.707107,0.707107;3.14159rad)
  Reference1 = -> Assembly [Body006.Face6,Body006.Face6]
  Reference2 = -> Assembly [Body002.Face5,Body002.Vertex6]
FEATURE [App::FeaturePython] Joint016  label="Distance007"  # Assembly joint (typed FeaturePython)
  Activated = true
  AngleMax = 0
  AngleMin = 0
  Detach1 = false
  Detach2 = false
  Distance = 0
  Distance2 = 0
  EnableAngleMax = false
  EnableAngleMin = false
  EnableLengthMax = false
  EnableLengthMin = false
  JointType = 5 (Distance)
  LengthMax = 0
  LengthMin = 0
  Placement1 = pos=(0,-25,0) rot=(-1,0,0;1.5708rad)
  Placement2 = pos=(-50,0,-55) rot=(-0.57735,0.57735,-0.57735;2.0944rad)
  Reference1 = -> Assembly [Body006.Face2,Body006.Vertex6]
  Reference2 = -> Assembly [Body002.Face1,Body002.Face1]
FEATURE [App::FeaturePython] Joint017  label="Distance008"  # Assembly joint (typed FeaturePython)
  Activated = true
  AngleMax = 0
  AngleMin = 0
  Detach1 = false
  Detach2 = false
  Distance = -100
  Distance2 = 0
  EnableAngleMax = false
  EnableAngleMin = false
  EnableLengthMax = false
  EnableLengthMin = false
  JointType = 5 (Distance)
  LengthMax = 0
  LengthMin = 0
  Placement1 = pos=(50,0,0) rot=(-0.57735,-0.57735,0.57735;2.0944rad)
  Placement2 = pos=(-2e-16,0,-410) rot=(0,0,1;0rad)
  Reference1 = -> Assembly [Body006.Face3,Body006.Vertex7]
  Reference2 = -> Assembly [Body.Face2,Body.Face2]
FEATURE [App::FeaturePython] Joint018  label="Distance009"  # Assembly joint (typed FeaturePython)
  Activated = true
  AngleMax = 0
  AngleMin = 0
  Detach1 = false
  Detach2 = false
  Distance = 0
  Distance2 = 0
  EnableAngleMax = false
  EnableAngleMin = false
  EnableLengthMax = false
  EnableLengthMin = false
  JointType = 5 (Distance)
  LengthMax = 0
  LengthMin = 0
  Placement1 = pos=(5.68e-14,1.137e-13,835) rot=(0,0,1;0rad)
  Placement2 = pos=(1.4676,50,-14.8856) rot=(0,-0.707107,0.707107;3.14159rad)
  Reference1 = -> Assembly [Body007.Face6,Body007.Face6]
  Reference2 = -> Assembly [Body001.Face5,Body001.Face5]
FEATURE [App::FeaturePython] Joint019  label="Distance010"  # Assembly joint (typed FeaturePython)
  Activated = true
  AngleMax = 0
  AngleMin = 0
  Detach1 = false
  Detach2 = false
  Distance = 0
  Distance2 = 0
  EnableAngleMax = false
  EnableAngleMin = false
  EnableLengthMax = false
  EnableLengthMin = false
  JointType = 5 (Distance)
  LengthMax = 0
  LengthMin = 0
  Placement1 = pos=(5.68e-14,-25,1.137e-13) rot=(-1,0,0;1.5708rad)
  Placement2 = pos=(-50,1e-15,-55) rot=(0.57735,-0.57735,0.57735;4.18879rad)
  Reference1 = -> Assembly [Body007.Face2,Body007.Vertex6]
  Reference2 = -> Assembly [Body001.Face1,Body001.Face1]
FEATURE [App::FeaturePython] Joint020  label="Distance011"  # Assembly joint (typed FeaturePython)
  Activated = true
  AngleMax = 0
  AngleMin = 0
  Detach1 = false
  Detach2 = false
  Distance = 0
  Distance2 = 0
  EnableAngleMax = false
  EnableAngleMin = false
  EnableLengthMax = false
  EnableLengthMin = false
  JointType = 5 (Distance)
  LengthMax = 0
  LengthMin = 0
  Placement1 = pos=(50,0,0) rot=(-0.57735,-0.57735,0.57735;2.0944rad)
  Placement2 = pos=(50,0,0) rot=(-0.57735,-0.57735,0.57735;2.0944rad)
  Reference1 = -> Assembly [Body006.Face3,Body006.Vertex7]
  Reference2 = -> Assembly [Body007.Face3,Body007.Vertex6]
FEATURE [Assembly::JointGroup] Joints
  Group = -> [GroundedJoint,Joint,Joint001,Joint002,Joint003,Joint004,Joint005,Joint006,Joint007,Joint008,Joint009,Joint010,Joint011,Joint012,Joint013,Joint014,Joint015,Joint016,Joint017,Joint018,Joint019,Joint020]
FEATURE [Assembly::AssemblyObject] Assembly
  Group = -> [Joints,Body,GroundedJoint,Body001,Joint,Joint001,Joint002,Body002,Joint003,Joint004,Joint005,Body003,Joint006,Joint007,Joint008,Body004,Body005,Joint009,Joint010,Joint011,Joint012,Joint013,Joint014,Body006,Body007,Joint015,Joint016,Joint017,Joint018,Joint019,Joint020]
  Origin = -> Origin
  Type = Assembly
